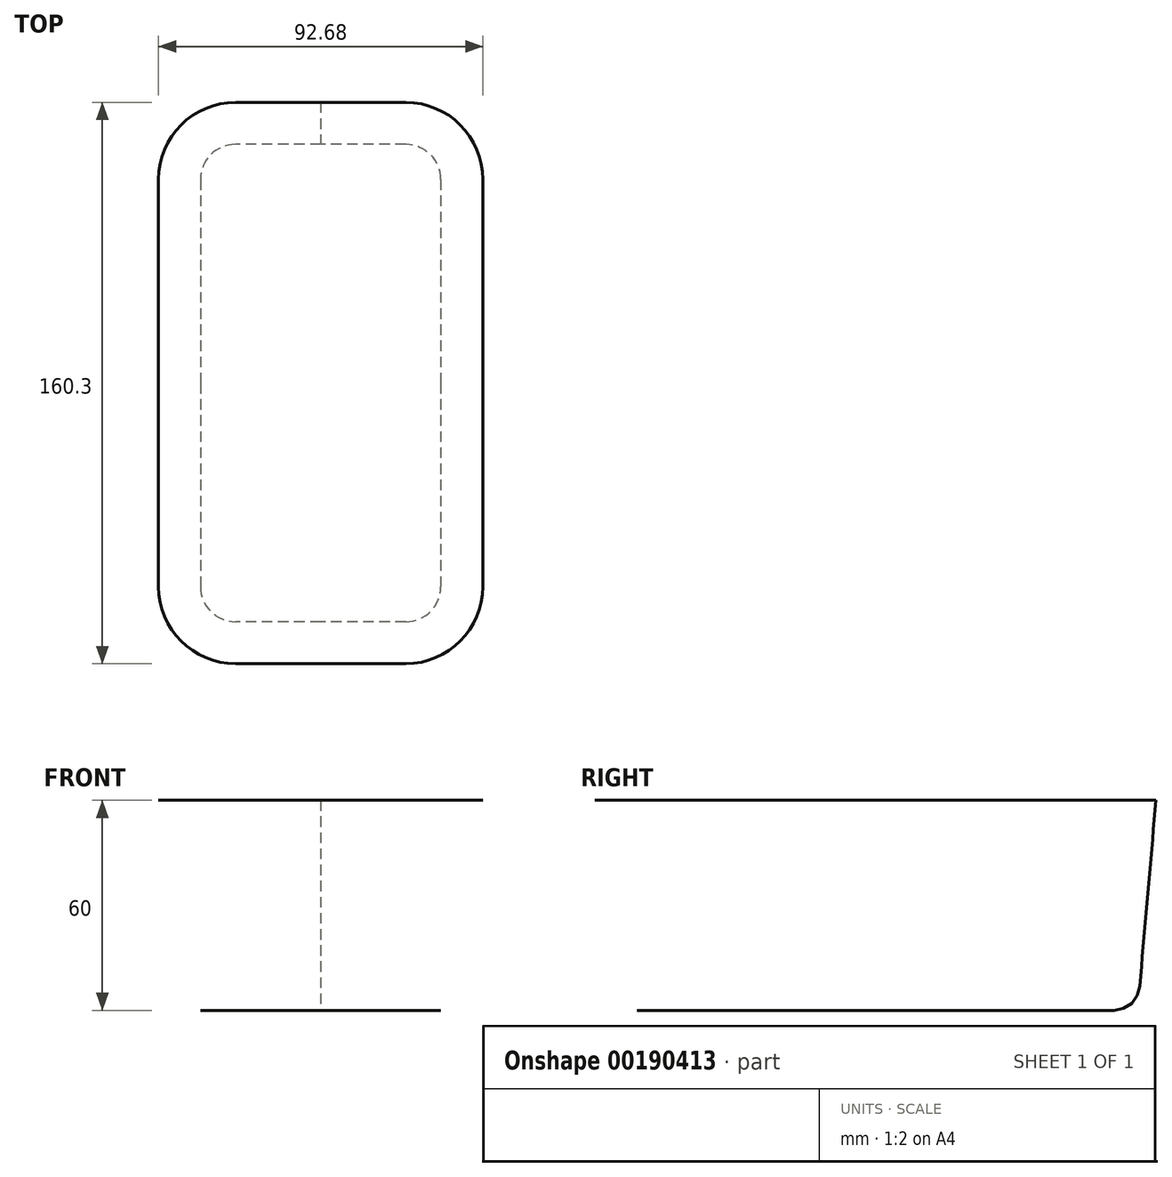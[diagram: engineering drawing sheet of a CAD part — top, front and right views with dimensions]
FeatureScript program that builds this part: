
annotation { "Feature Type Name" : "Feature", "Feature Type Description" : "" }
export const myFeature = defineFeature(function(context is Context, id is Id, definition is map)
    precondition{}
    {
        {
            var Q0;
            Q0=qCreatedBy(makeId("Top.planeOp"),FACE);
            var sketch = newSketch(context, id + "F0", { "sketchPlane" : qUnion([Q0])});
            skLineSegment(sketch, "E0.bottom", {"start": v(24.34, 68.15) * mm, "end": v(-24.34, 68.15) * mm});
            skLineSegment(sketch, "E0.top", {"start": v(24.34, -68.15) * mm, "end": v(-24.34, -68.15) * mm});
            skLineSegment(sketch, "E0.left", {"start": v(34.34, 58.15) * mm, "end": v(34.34, -58.15) * mm});
            skLineSegment(sketch, "E0.right", {"start": v(-34.34, 58.15) * mm, "end": v(-34.34, -58.15) * mm});
            skPoint(sketch, "E0.middle", {"position": v(0, 0) * mm});
            skPoint(sketch, "E1.visualSharp", {"position": v(-34.34, 68.15) * mm});
            skArc(sketch, "E1.filletArc", {"start": v(-24.34, 68.15) * mm, "mid": v(-31.4, 65.22) * mm, "end": v(-34.34, 58.15) * mm});
            skPoint(sketch, "E2.visualSharp", {"position": v(34.34, 68.15) * mm});
            skArc(sketch, "E2.filletArc", {"start": v(34.34, 58.15) * mm, "mid": v(31.4, 65.22) * mm, "end": v(24.34, 68.15) * mm});
            skPoint(sketch, "E3.visualSharp", {"position": v(34.34, -68.15) * mm});
            skArc(sketch, "E3.filletArc", {"start": v(24.34, -68.15) * mm, "mid": v(31.4, -65.22) * mm, "end": v(34.34, -58.15) * mm});
            skPoint(sketch, "E4.visualSharp", {"position": v(-34.34, -68.15) * mm});
            skArc(sketch, "E4.filletArc", {"start": v(-34.34, -58.15) * mm, "mid": v(-31.4, -65.22) * mm, "end": v(-24.34, -68.15) * mm});
            skSolve(sketch);
        }
        {
            var Q0;
            Q0=qCreatedBy(makeId("Top.planeOp"),FACE);
            cPlane(context, id + "F1", {"entities" : qUnion([Q0]), "cplaneType" : CPlaneType.OFFSET, "offset" : 60 * mm, "width" : 150 * mm, "height" : 150 * mm});
        }
        {
            var Q0;
            Q0=qCreatedBy(id+"F1.planeOp",FACE);
            var sketch = newSketch(context, id + "F2", { "sketchPlane" : qUnion([Q0])});
            skArc(sketch, "E5.0", {"start": v(-24.34, 80.15) * mm, "mid": v(-39.9, 73.7) * mm, "end": v(-46.34, 58.15) * mm});
            skLineSegment(sketch, "E5.1", {"start": v(24.34, 80.15) * mm, "end": v(-24.34, 80.15) * mm});
            skLineSegment(sketch, "E5.2", {"start": v(-46.34, 58.15) * mm, "end": v(-46.34, -58.15) * mm});
            skArc(sketch, "E5.3", {"start": v(46.34, 58.15) * mm, "mid": v(39.9, 73.7) * mm, "end": v(24.34, 80.15) * mm});
            skArc(sketch, "E5.4", {"start": v(-46.34, -58.15) * mm, "mid": v(-39.9, -73.7) * mm, "end": v(-24.34, -80.15) * mm});
            skLineSegment(sketch, "E5.5", {"start": v(24.34, -80.15) * mm, "end": v(-24.34, -80.15) * mm});
            skArc(sketch, "E5.6", {"start": v(24.34, -80.15) * mm, "mid": v(39.9, -73.7) * mm, "end": v(46.34, -58.15) * mm});
            skLineSegment(sketch, "E5.7", {"start": v(46.34, 58.15) * mm, "end": v(46.34, -58.15) * mm});
            skSolve(sketch);
        }
        {
            var Q0;
            Q0=qCreatedBy(makeId("Front.planeOp"),FACE);
            var sketch = newSketch(context, id + "F3", { "sketchPlane" : qUnion([Q0])});
            skLineSegment(sketch, "E6", {"start": v(-46.34, 60) * mm, "end": v(-41.68, 6.72) * mm});
            skArc(sketch, "E7", {"start": v(-41.68, 6.72) * mm, "mid": v(-39.31, 1.94) * mm, "end": v(-34.34, 0) * mm});
            skSolve(sketch);
        }
        {
            var Q0;
            Q0=qCreatedBy(makeId("Front.planeOp"),FACE);
            var sketch = newSketch(context, id + "F4", { "sketchPlane" : qUnion([Q0])});
            skLineSegment(sketch, "E8", {"start": v(0, 0) * mm, "end": v(0, 72.91) * mm, "construction": true});
            skLineSegment(sketch, "E9", {"start": v(46.34, 60) * mm, "end": v(41.68, 6.72) * mm});
            skArc(sketch, "E10", {"start": v(41.68, 6.72) * mm, "mid": v(39.31, 1.94) * mm, "end": v(34.34, 0) * mm});
            skSolve(sketch);
        }
        {
            var Q0;
            Q0=qCreatedBy(makeId("Right.planeOp"),FACE);
            var sketch = newSketch(context, id + "F5", { "sketchPlane" : qUnion([Q0])});
            skLineSegment(sketch, "E11", {"start": v(-80.15, 60) * mm, "end": v(-75.49, 6.72) * mm});
            skArc(sketch, "E12", {"start": v(-75.49, 6.72) * mm, "mid": v(-73.12, 1.94) * mm, "end": v(-68.15, 0) * mm});
            skSolve(sketch);
        }
        {
            var Q0;
            Q0=qCreatedBy(makeId("Right.planeOp"),FACE);
            var sketch = newSketch(context, id + "F6", { "sketchPlane" : qUnion([Q0])});
            skLineSegment(sketch, "E13", {"start": v(80.15, 60) * mm, "end": v(75.49, 6.72) * mm});
            skArc(sketch, "E14", {"start": v(75.49, 6.72) * mm, "mid": v(73.12, 1.94) * mm, "end": v(68.15, 0) * mm});
            skSolve(sketch);
        }
        {
            var Q0;
            Q0=makeQuery(id+"F2.imprint","IMPRINT",FACE,{"disambiguationData":[TD([[makeQuery(id+"F2.imprint","IMPRINT",EDGE,{"derivedFrom":sQuery(id+"F2.wireOp",EDGE,"E5.0")}),1.0]])]});
            var Q1;
            Q1=makeQuery(id+"F0.imprint","IMPRINT",FACE,{"disambiguationData":[TD([[makeQuery(id+"F0.imprint","IMPRINT",EDGE,{"derivedFrom":sQuery(id+"F0.wireOp",EDGE,"E0.bottom")}),1.0]])]});
            var Q2;
            Q2 = qConstructionFilter(qBodyType(qCreatedBy(id + "F3" ,EDGE), BodyType.WIRE), ConstructionObject.NO);
            var Q3;
            Q3 = qConstructionFilter(qBodyType(qCreatedBy(id + "F4" ,EDGE), BodyType.WIRE), ConstructionObject.NO);
            var Q4;
            Q4 = qConstructionFilter(qBodyType(qCreatedBy(id + "F5" ,EDGE), BodyType.WIRE), ConstructionObject.NO);
            var Q5;
            Q5 = qConstructionFilter(qBodyType(qCreatedBy(id + "F6" ,EDGE), BodyType.WIRE), ConstructionObject.NO);
            loft(context, id + "F7", {"addGuides" : true, "sheetProfilesArray" : [{ "sheetProfileEntities" : qUnion([Q0]) }, { "sheetProfileEntities" : qUnion([Q1]) }], "guidesArray" : [{ "guideEntities" : qUnion([Q2]), "guideDerivativeType" : LoftGuideDerivativeType.DEFAULT, "guideDerivativeMagnitude" : 1 }, { "guideEntities" : qUnion([Q3]), "guideDerivativeType" : LoftGuideDerivativeType.DEFAULT, "guideDerivativeMagnitude" : 1 }, { "guideEntities" : qUnion([Q4]), "guideDerivativeType" : LoftGuideDerivativeType.DEFAULT, "guideDerivativeMagnitude" : 1 }, { "guideEntities" : qUnion([Q5]), "guideDerivativeType" : LoftGuideDerivativeType.DEFAULT, "guideDerivativeMagnitude" : 1 }]});
        }
    });
